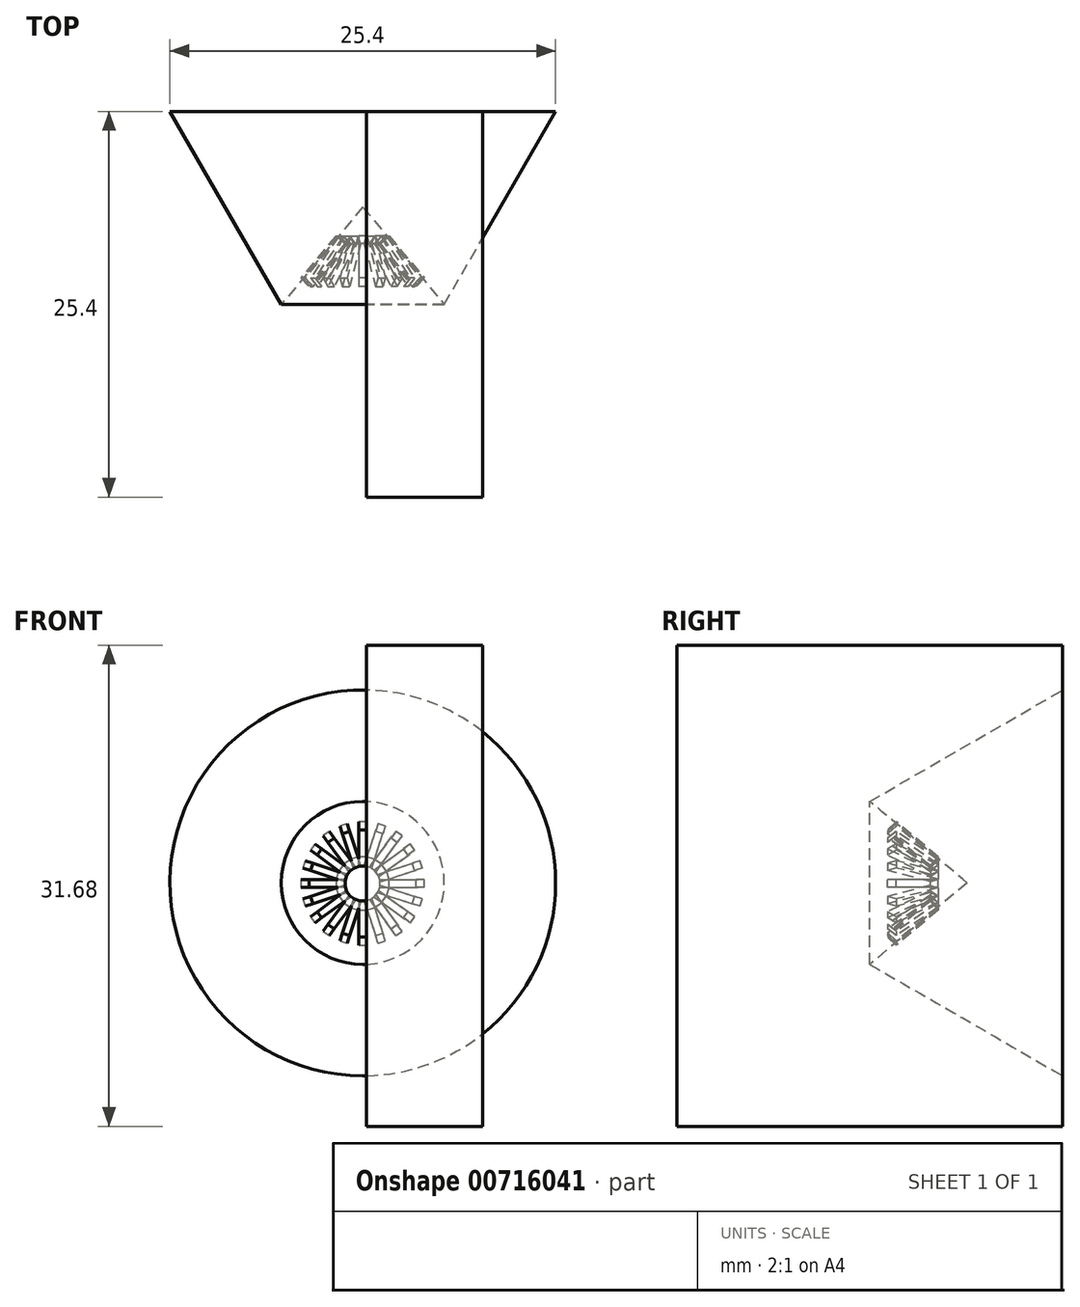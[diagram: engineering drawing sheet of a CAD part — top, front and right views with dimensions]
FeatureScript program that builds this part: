
annotation { "Feature Type Name" : "Feature", "Feature Type Description" : "" }
export const myFeature = defineFeature(function(context is Context, id is Id, definition is map)
    precondition{}
    {
        {
            var Q0;
            Q0=qCreatedBy(makeId("Front.planeOp"),FACE);
            var sketch = newSketch(context, id + "F0", { "sketchPlane" : qUnion([Q0])});
            skLineSegment(sketch, "E0", {"start": v(0, 51.45) * mm, "end": v(0, -50.15) * mm, "construction": true});
            skLineSegment(sketch, "E1", {"start": v(12.71, 0.04) * mm, "end": v(-12.69, 0.04) * mm});
            skCircle(sketch, "E2", {"center": v(0.01, 0.04) * mm, "radius": 12.7 * mm});
            skCircle(sketch, "E3", {"center": v(0.01, 0.04) * mm, "radius": 10.16 * mm});
            skSolve(sketch);
        }
        {
            var Q0;
            Q0=qSketchRegion(id+"F0",true);
            var Q1;
            {var subQ0=sQuery(id+"F0.wireOp",EDGE,"E3");var subQ1=sQuery(id+"F0.wireOp",EDGE,"E1");var subQ2=makeQuery(id+"F0.imprint","INTERSECT",VERTEX,{"disambiguationData":[OD(0.0)],"derivedFrom":[subQ1,subQ0]});Q1=makeQuery(id+"F0.imprint","IMPRINT",FACE,{"disambiguationData":[TD([[makeQuery(id+"F0.imprint","IMPRINT",EDGE,{"disambiguationData":[TD([[subQ2,-1.0]])],"derivedFrom":subQ1}),-1.0]])]});}
            var Q2;
            {var subQ0=sQuery(id+"F0.wireOp",EDGE,"E3");var subQ1=sQuery(id+"F0.wireOp",EDGE,"E1");var subQ2=makeQuery(id+"F0.imprint","INTERSECT",VERTEX,{"disambiguationData":[OD(0.0)],"derivedFrom":[subQ1,subQ0]});Q2=makeQuery(id+"F0.imprint","IMPRINT",FACE,{"disambiguationData":[TD([[makeQuery(id+"F0.imprint","IMPRINT",EDGE,{"disambiguationData":[TD([[subQ2,-1.0]])],"derivedFrom":subQ1}),1.0]])]});}
            extrude(context, id + "F1", {"entities" : qUnion([Q0, Q1, Q2]), "depth" : 12.7 * mm, "offsetDistance" : 25.4 * mm, "hasDraft" : true, "draftAngle" : 30 * degree, "draftPullDirection" : true});
        }
        {
            var Q0;
            Q0=makeQuery(id+"F1.opExtrude","CAP_FACE",FACE,{"disambiguationData":[OSD([sQuery(id+"F0.wireOp",EDGE,"E2")])],"isStart":false});
            extrude(context, id + "F2", {"entities" : qUnion([Q0]), "operationType" : NewBodyOperationType.REMOVE, "oppositeDirection" : true, "depth" : 7.62 * mm, "offsetDistance" : 25.4 * mm, "hasDraft" : true, "draftAngle" : 40 * degree, "draftPullDirection" : true});
        }
        {
            var Q0;
            Q0=qCreatedBy(makeId("Front.planeOp"),FACE);
            var sketch = newSketch(context, id + "F3", { "sketchPlane" : qUnion([Q0])});
            skLineSegment(sketch, "E4.bottom", {"start": v(0.25, 15.7) * mm, "end": v(7.9, 15.7) * mm});
            skLineSegment(sketch, "E4.top", {"start": v(0.25, -15.99) * mm, "end": v(7.9, -15.99) * mm});
            skLineSegment(sketch, "E4.left", {"start": v(0.25, 15.7) * mm, "end": v(0.25, -15.99) * mm});
            skLineSegment(sketch, "E4.right", {"start": v(7.9, 15.7) * mm, "end": v(7.9, -15.99) * mm});
            skSolve(sketch);
        }
        {
            var Q0;
            Q0=qSketchRegion(id+"F3",true);
            extrude(context, id + "F4", {"entities" : qUnion([Q0]), "depth" : 25.4 * mm, "offsetDistance" : 25.4 * mm});
        }
        {
            var Q0;
            Q0=makeQuery(id+"F4.opExtrude","SWEPT_FACE",FACE,{"disambiguationData":[OSD([sQuery(id+"F3.wireOp",EDGE,"E4.left")])]});
            var sketch = newSketch(context, id + "F5", { "sketchPlane" : qUnion([Q0])});
            skLineSegment(sketch, "E5", {"start": v(8.72, -1.14) * mm, "end": v(11.54, -3.51) * mm});
            skLineSegment(sketch, "E6", {"start": v(8.72, -1.14) * mm, "end": v(8.2, -1.75) * mm});
            skLineSegment(sketch, "E7", {"start": v(8.2, -1.75) * mm, "end": v(10.95, -4.06) * mm});
            skLineSegment(sketch, "E8", {"start": v(10.95, -4.06) * mm, "end": v(11.54, -3.51) * mm});
            skSolve(sketch);
        }
        {
            var Q0;
            Q0=qSketchRegion(id+"F5",true);
            extrude(context, id + "F6", {"entities" : qUnion([Q0]), "depth" : 0.5 * mm, "offsetDistance" : 25.4 * mm});
        }
        {
            var Q0;
            Q0=qCreatedBy(makeId("Right.planeOp"),FACE);
            var sketch = newSketch(context, id + "F7", { "sketchPlane" : qUnion([Q0])});
            skLineSegment(sketch, "E9", {"start": v(0, 0) * mm, "end": v(-21.25, 0) * mm});
            skSolve(sketch);
        }
        {
            var Q0;
            Q0=makeQuery(id+"F6.opExtrude","SWEPT_BODY",BODY,{"disambiguationData":[OSD([sQuery(id+"F5.wireOp",EDGE,"E5"),sQuery(id+"F5.wireOp",EDGE,"E6"),sQuery(id+"F5.wireOp",EDGE,"E7"),sQuery(id+"F5.wireOp",EDGE,"E8")])]});
            var Q1;
            Q1=sQuery(id+"F7.wireOp",EDGE,"E9");
            circularPattern(context, id + "F8", {"entities" : qUnion([Q0]), "axis" : qUnion([Q1]), "angle" : 360 * degree, "instanceCount" : 20, "equalSpace" : true});
        }
    });
